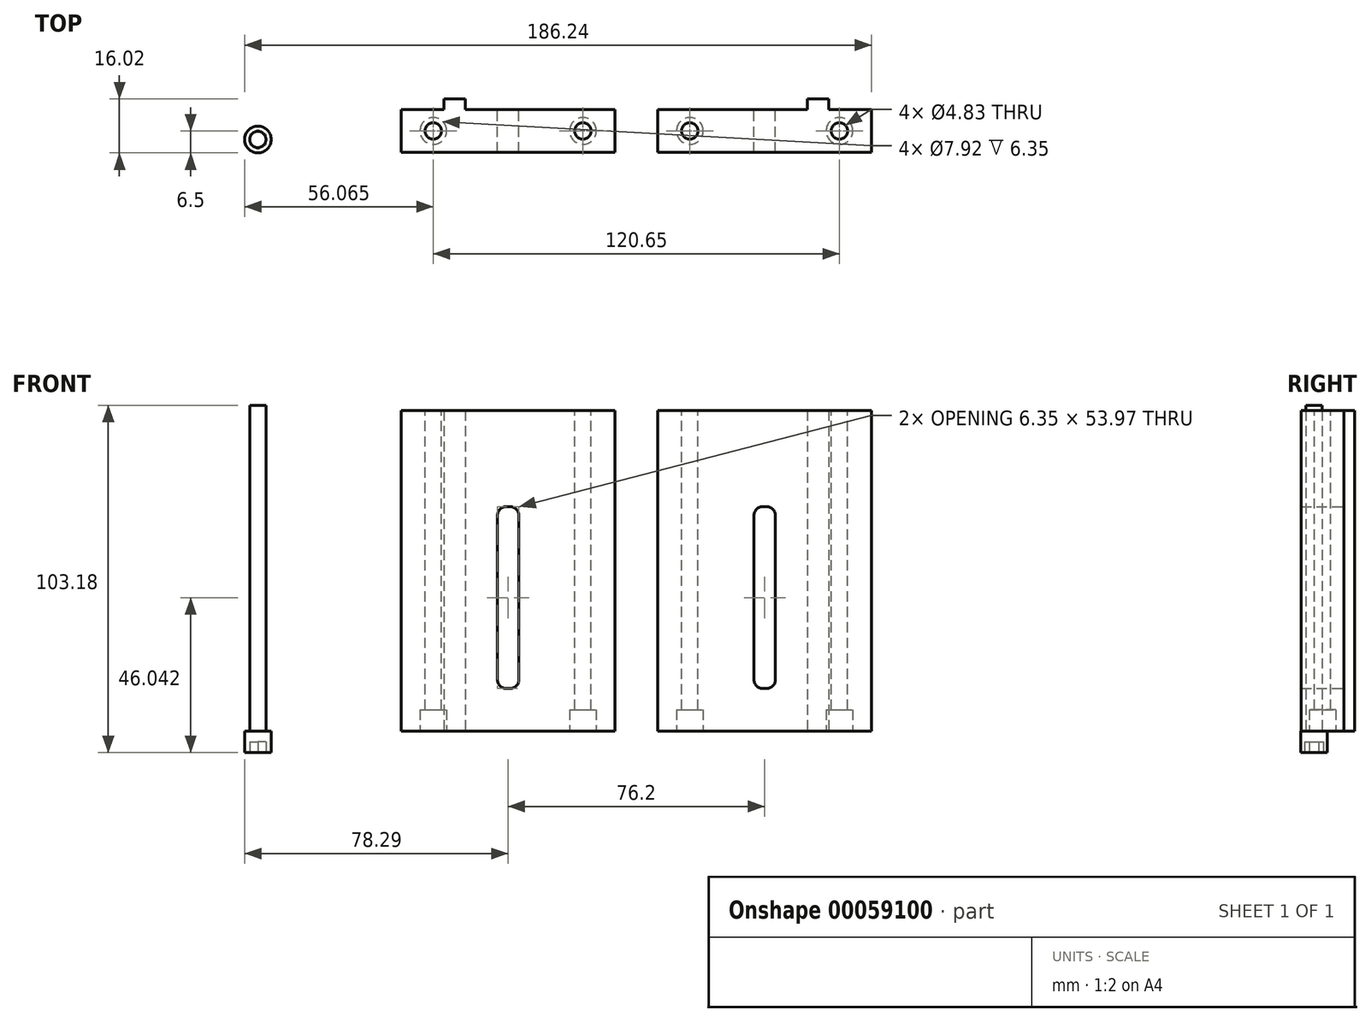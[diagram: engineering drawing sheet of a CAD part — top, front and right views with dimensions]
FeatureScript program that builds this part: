
annotation { "Feature Type Name" : "Feature", "Feature Type Description" : "" }
export const myFeature = defineFeature(function(context is Context, id is Id, definition is map)
    precondition{}
    {
        {
            var Q0;
            Q0=qCreatedBy(makeId("Front.planeOp"),FACE);
            var sketch = newSketch(context, id + "F0", { "sketchPlane" : qUnion([Q0])});
            skLineSegment(sketch, "E0.rect.bottom", {"start": v(31.75, -47.62) * mm, "end": v(-31.75, -47.63) * mm});
            skLineSegment(sketch, "E0.rect.top", {"start": v(31.75, 47.63) * mm, "end": v(-31.75, 47.62) * mm});
            skLineSegment(sketch, "E0.rect.left", {"start": v(31.75, -47.62) * mm, "end": v(31.75, 47.63) * mm});
            skLineSegment(sketch, "E0.rect.right", {"start": v(-31.75, -47.63) * mm, "end": v(-31.75, 47.62) * mm});
            skPoint(sketch, "E0.rect.middle", {"position": v(0, 0) * mm});
            skLineSegment(sketch, "E1.rect.bottom", {"start": v(3.18, 19.05) * mm, "end": v(-3.17, 19.05) * mm});
            skLineSegment(sketch, "E1.rect.top", {"start": v(3.18, -34.92) * mm, "end": v(-3.17, -34.92) * mm});
            skLineSegment(sketch, "E1.rect.left", {"start": v(3.18, 19.05) * mm, "end": v(3.18, -34.92) * mm});
            skLineSegment(sketch, "E1.rect.right", {"start": v(-3.17, 19.05) * mm, "end": v(-3.17, -34.92) * mm});
            skLineSegment(sketch, "E2", {"start": v(-31.75, 0) * mm, "end": v(31.75, 0) * mm, "construction": true});
            skSolve(sketch);
        }
        {
            var Q0;
            Q0=makeQuery(id+"F0.imprint","IMPRINT",FACE,{"disambiguationData":[TD([[makeQuery(id+"F0.imprint","IMPRINT",EDGE,{"derivedFrom":sQuery(id+"F0.wireOp",EDGE,"E0.rect.bottom")}),-1.0]])]});
            extrude(context, id + "F1", {"entities" : qUnion([Q0]), "depth" : 12.7 * mm});
        }
        {
            var Q0;
            Q0=makeQuery(id+"F1.opExtrude","SWEPT_EDGE",EDGE,{"disambiguationData":[OSD([sQuery(id+"F0.wireOp",EDGE,"E1.rect.bottom"),sQuery(id+"F0.wireOp",EDGE,"E1.rect.right")])]});
            var Q1;
            Q1=makeQuery(id+"F1.opExtrude","SWEPT_EDGE",EDGE,{"disambiguationData":[OSD([sQuery(id+"F0.wireOp",EDGE,"E1.rect.bottom"),sQuery(id+"F0.wireOp",EDGE,"E1.rect.left")])]});
            var Q2;
            Q2=makeQuery(id+"F1.opExtrude","SWEPT_EDGE",EDGE,{"disambiguationData":[OSD([sQuery(id+"F0.wireOp",EDGE,"E1.rect.top"),sQuery(id+"F0.wireOp",EDGE,"E1.rect.left")])]});
            var Q3;
            Q3=makeQuery(id+"F1.opExtrude","SWEPT_EDGE",EDGE,{"disambiguationData":[OSD([sQuery(id+"F0.wireOp",EDGE,"E1.rect.top"),sQuery(id+"F0.wireOp",EDGE,"E1.rect.right")])]});
            fillet(context, id + "F2", {"entities" : qUnion([Q0, Q1, Q2, Q3]), "radius" : 2.54 * mm, "tangentPropagation" : true, "allowEdgeOverflow" : false});
        }
        {
            var Q0;
            {var subQ0=sQuery(id+"F0.wireOp",EDGE,"E0.rect.top");Q0=makeQuery(id+"F9.boolean.opBoolean","MERGE",FACE,{"derivedFrom":[makeQuery(id+"F1.opExtrude","SWEPT_FACE",FACE,{"disambiguationData":[OSD([subQ0])]}),makeQuery(id+"F9.opExtrude","SWEPT_FACE",FACE,{"disambiguationData":[OSD([subQ0])]})]});}
            var sketch = newSketch(context, id + "F3", { "sketchPlane" : qUnion([Q0])});
            skLineSegment(sketch, "E3", {"start": v(-31.75, -6.35) * mm, "end": v(31.75, -6.35) * mm, "construction": true});
            skLineSegment(sketch, "E4", {"start": v(-22.23, 0) * mm, "end": v(-22.23, -12.7) * mm, "construction": true});
            skLineSegment(sketch, "E5", {"start": v(22.23, 0) * mm, "end": v(22.23, -12.7) * mm, "construction": true});
            skCircle(sketch, "E6", {"center": v(-22.23, -6.35) * mm, "radius": 2.41 * mm});
            skCircle(sketch, "E7", {"center": v(22.23, -6.35) * mm, "radius": 2.41 * mm});
            skSolve(sketch);
        }
        {
            var Q0;
            Q0=makeQuery(id+"F3.imprint","IMPRINT",FACE,{"disambiguationData":[TD([[makeQuery(id+"F3.imprint","IMPRINT",EDGE,{"derivedFrom":sQuery(id+"F3.wireOp",EDGE,"E6")}),1.0]])]});
            var Q1;
            Q1=makeQuery(id+"F3.imprint","IMPRINT",FACE,{"disambiguationData":[TD([[makeQuery(id+"F3.imprint","IMPRINT",EDGE,{"derivedFrom":sQuery(id+"F3.wireOp",EDGE,"E7")}),1.0]])]});
            extrude(context, id + "F4", {"entities" : qUnion([Q0, Q1]), "operationType" : NewBodyOperationType.REMOVE, "endBound" : BoundingType.THROUGH_ALL, "oppositeDirection" : true, "depth" : 25.4 * mm});
        }
        {
            var Q0;
            {var subQ0=sQuery(id+"F0.wireOp",EDGE,"E0.rect.bottom");Q0=makeQuery(id+"F9.boolean.opBoolean","MERGE",FACE,{"derivedFrom":[makeQuery(id+"F1.opExtrude","SWEPT_FACE",FACE,{"disambiguationData":[OSD([subQ0])]}),makeQuery(id+"F9.opExtrude","SWEPT_FACE",FACE,{"disambiguationData":[OSD([subQ0])]})]});}
            var sketch = newSketch(context, id + "F5", { "sketchPlane" : qUnion([Q0])});
            skCircle(sketch, "E8", {"center": v(-22.22, 6.35) * mm, "radius": 3.96 * mm});
            skCircle(sketch, "E9", {"center": v(22.23, 6.35) * mm, "radius": 3.96 * mm});
            skSolve(sketch);
        }
        {
            var Q0;
            Q0=makeQuery(id+"F5.imprint","IMPRINT",FACE,{"disambiguationData":[TD([[makeQuery(id+"F5.imprint","IMPRINT",EDGE,{"derivedFrom":sQuery(id+"F5.wireOp",EDGE,"E8")}),1.0]])]});
            var Q1;
            Q1=makeQuery(id+"F5.imprint","IMPRINT",FACE,{"disambiguationData":[TD([[makeQuery(id+"F5.imprint","IMPRINT",EDGE,{"derivedFrom":sQuery(id+"F5.wireOp",EDGE,"E9")}),1.0]])]});
            extrude(context, id + "F6", {"entities" : qUnion([Q0, Q1]), "operationType" : NewBodyOperationType.REMOVE, "oppositeDirection" : true, "depth" : 6.35 * mm});
        }
        {
            var Q0;
            Q0=makeQuery(id+"F1.opExtrude","SWEPT_BODY",BODY,{"disambiguationData":[OSD([sQuery(id+"F0.wireOp",EDGE,"E0.rect.bottom"),sQuery(id+"F0.wireOp",EDGE,"E0.rect.top"),sQuery(id+"F0.wireOp",EDGE,"E0.rect.left"),sQuery(id+"F0.wireOp",EDGE,"E0.rect.right"),sQuery(id+"F0.wireOp",EDGE,"E1.rect.bottom"),sQuery(id+"F0.wireOp",EDGE,"E1.rect.top"),sQuery(id+"F0.wireOp",EDGE,"E1.rect.left"),sQuery(id+"F0.wireOp",EDGE,"E1.rect.right")])]});
            var Q1;
            Q1=makeQuery(id+"F1.opExtrude","SWEPT_FACE",FACE,{"disambiguationData":[OSD([sQuery(id+"F0.wireOp",EDGE,"E0.rect.left")])]});
            transform(context, id + "F7", {"entities" : qUnion([Q0]), "transformType" : TransformType.TRANSLATION_DISTANCE, "transformDirection" : qUnion([Q1]), "distance" : 76.2 * mm, "makeCopy" : true});
        }
        {
            var Q0;
            Q0=makeQuery(id+"F1.opExtrude","CAP_FACE",FACE,{"disambiguationData":[OSD([sQuery(id+"F0.wireOp",EDGE,"E0.rect.bottom"),sQuery(id+"F0.wireOp",EDGE,"E0.rect.top"),sQuery(id+"F0.wireOp",EDGE,"E0.rect.left"),sQuery(id+"F0.wireOp",EDGE,"E0.rect.right"),sQuery(id+"F0.wireOp",EDGE,"E1.rect.bottom"),sQuery(id+"F0.wireOp",EDGE,"E1.rect.top"),sQuery(id+"F0.wireOp",EDGE,"E1.rect.left"),sQuery(id+"F0.wireOp",EDGE,"E1.rect.right")])],"isStart":true});
            var sketch = newSketch(context, id + "F8", { "sketchPlane" : qUnion([Q0])});
            skLineSegment(sketch, "E10", {"start": v(12.7, 47.63) * mm, "end": v(12.7, -47.63) * mm});
            skLineSegment(sketch, "E11", {"start": v(19.05, 47.63) * mm, "end": v(19.05, -47.63) * mm});
            skLineSegment(sketch, "E12.0.0", {"start": v(-107.95, -47.63) * mm, "end": v(-44.45, -47.63) * mm});
            skLineSegment(sketch, "E12.0.1", {"start": v(-44.45, -47.63) * mm, "end": v(-44.45, 47.62) * mm});
            skLineSegment(sketch, "E12.0.2", {"start": v(-44.45, 47.62) * mm, "end": v(-107.95, 47.63) * mm});
            skLineSegment(sketch, "E12.0.3", {"start": v(-107.95, 47.63) * mm, "end": v(-107.95, -47.62) * mm});
            skLineSegment(sketch, "E13", {"start": v(-95.25, 47.62) * mm, "end": v(-95.25, -47.63) * mm});
            skLineSegment(sketch, "E14", {"start": v(-88.9, 47.62) * mm, "end": v(-88.9, -47.63) * mm});
            skSolve(sketch);
        }
        {
            var Q0;
            {var subQ0=sQuery(id+"F8.wireOp",EDGE,"E10");Q0=makeQuery(id+"F8.imprint","IMPRINT",FACE,{"disambiguationData":[TD([[makeQuery(id+"F8.imprint","IMPRINT",EDGE,{"derivedFrom":subQ0}),1.0]])]});}
            var Q1;
            {var subQ0=sQuery(id+"F8.wireOp",EDGE,"E13");Q1=makeQuery(id+"F8.imprint","IMPRINT",FACE,{"disambiguationData":[TD([[makeQuery(id+"F8.imprint","IMPRINT",EDGE,{"derivedFrom":subQ0}),1.0]])]});}
            extrude(context, id + "F9", {"entities" : qUnion([Q0, Q1]), "operationType" : NewBodyOperationType.ADD, "depth" : 3.17 * mm});
        }
        {
            var Q0;
            {var subQ0=sQuery(id+"F0.wireOp",EDGE,"E0.rect.bottom");Q0=makeQuery(id+"F9.boolean.opBoolean","MERGE",FACE,{"derivedFrom":[makeQuery(id+"F1.opExtrude","SWEPT_FACE",FACE,{"disambiguationData":[OSD([subQ0])]}),makeQuery(id+"F9.opExtrude","SWEPT_FACE",FACE,{"disambiguationData":[OSD([subQ0])]})]});}
            var sketch = newSketch(context, id + "F10", { "sketchPlane" : qUnion([Q0])});
            skCircle(sketch, "E15", {"center": v(-74.33, 8.9) * mm, "radius": 3.96 * mm});
            skSolve(sketch);
        }
        {
            var Q0;
            Q0=makeQuery(id+"F10.imprint","IMPRINT",FACE,{"disambiguationData":[TD([[makeQuery(id+"F10.imprint","IMPRINT",EDGE,{"derivedFrom":sQuery(id+"F10.wireOp",EDGE,"E15")}),1.0]])]});
            extrude(context, id + "F11", {"entities" : qUnion([Q0]), "depth" : 6.35 * mm});
        }
        {
            var Q0;
            Q0=makeQuery(id+"F11.opExtrude","CAP_FACE",FACE,{"disambiguationData":[OSD([sQuery(id+"F10.wireOp",EDGE,"E15")])],"isStart":false});
            var sketch = newSketch(context, id + "F12", { "sketchPlane" : qUnion([Q0])});
            skCircle(sketch, "E16.cCircle", {"center": v(-74.33, 8.9) * mm, "radius": 2.37 * mm, "construction": true});
            skLineSegment(sketch, "E16.0", {"start": v(-71.95, 7.52) * mm, "end": v(-74.33, 6.15) * mm});
            skLineSegment(sketch, "E16.1", {"start": v(-74.33, 6.15) * mm, "end": v(-76.7, 7.52) * mm});
            skLineSegment(sketch, "E16.2", {"start": v(-76.7, 7.52) * mm, "end": v(-76.7, 10.26) * mm});
            skLineSegment(sketch, "E16.3", {"start": v(-76.7, 10.26) * mm, "end": v(-74.33, 11.63) * mm});
            skLineSegment(sketch, "E16.4", {"start": v(-74.33, 11.63) * mm, "end": v(-71.95, 10.26) * mm});
            skLineSegment(sketch, "E16.5", {"start": v(-71.95, 10.26) * mm, "end": v(-71.95, 7.52) * mm});
            skPoint(sketch, "E16.0.midPoint", {"position": v(-73.14, 6.83) * mm});
            skSolve(sketch);
        }
        {
            var Q0;
            Q0=makeQuery(id+"F12.imprint","IMPRINT",FACE,{"disambiguationData":[TD([[makeQuery(id+"F12.imprint","IMPRINT",EDGE,{"derivedFrom":sQuery(id+"F12.wireOp",EDGE,"E16.0")}),-1.0]])]});
            extrude(context, id + "F13", {"entities" : qUnion([Q0]), "operationType" : NewBodyOperationType.REMOVE, "oppositeDirection" : true, "depth" : 3.17 * mm});
        }
        {
            var Q0;
            Q0=makeQuery(id+"F11.opExtrude","CAP_FACE",FACE,{"disambiguationData":[OSD([sQuery(id+"F10.wireOp",EDGE,"E15")])],"isStart":true});
            var sketch = newSketch(context, id + "F14", { "sketchPlane" : qUnion([Q0])});
            skCircle(sketch, "E17", {"center": v(-74.33, -8.9) * mm, "radius": 2.41 * mm});
            skSolve(sketch);
        }
        {
            var Q0;
            Q0=makeQuery(id+"F14.imprint","IMPRINT",FACE,{"disambiguationData":[TD([[makeQuery(id+"F14.imprint","IMPRINT",EDGE,{"derivedFrom":sQuery(id+"F14.wireOp",EDGE,"E17")}),1.0]])]});
            extrude(context, id + "F15", {"entities" : qUnion([Q0]), "operationType" : NewBodyOperationType.ADD, "depth" : 96.82 * mm});
        }
    });
